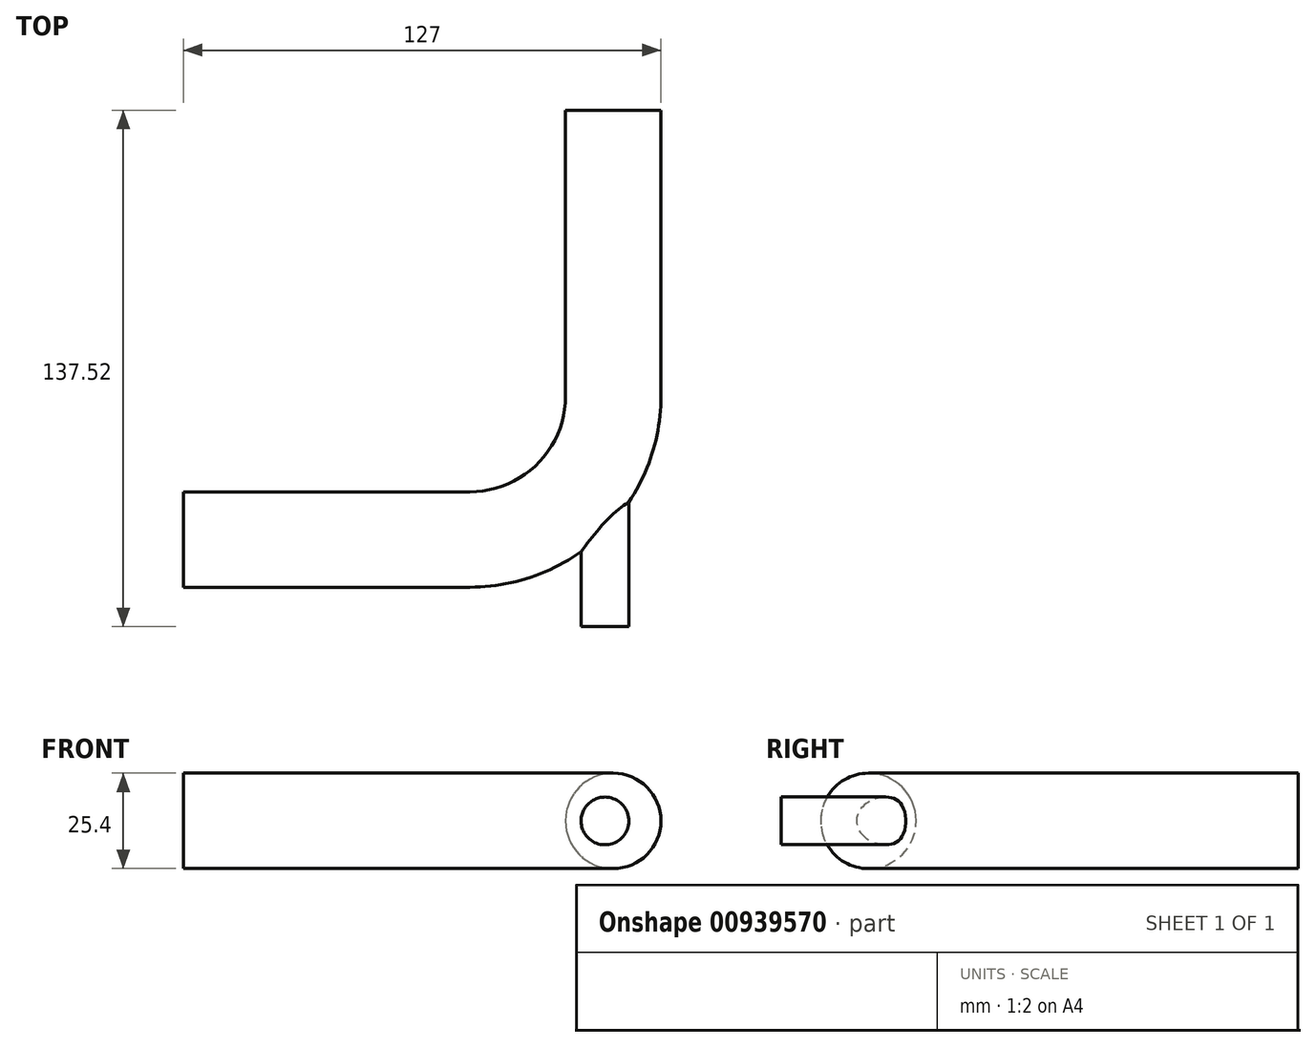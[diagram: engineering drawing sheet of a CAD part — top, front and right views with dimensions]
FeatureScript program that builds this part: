
annotation { "Feature Type Name" : "Feature", "Feature Type Description" : "" }
export const myFeature = defineFeature(function(context is Context, id is Id, definition is map)
    precondition{}
    {
        {
            var Q0;
            Q0=qCreatedBy(makeId("Top.planeOp"),FACE);
            var sketch = newSketch(context, id + "F0", { "sketchPlane" : qUnion([Q0])});
            skLineSegment(sketch, "E0", {"start": v(0, 0) * mm, "end": v(76.2, 0) * mm});
            skArc(sketch, "E1", {"start": v(76.2, 0) * mm, "mid": v(103.14, 11.16) * mm, "end": v(114.3, 38.1) * mm});
            skLineSegment(sketch, "E2", {"start": v(114.3, 38.1) * mm, "end": v(114.3, 114.3) * mm});
            skArc(sketch, "E3.0", {"start": v(76.2, -12.7) * mm, "mid": v(112.12, 2.18) * mm, "end": v(127, 38.1) * mm, "construction": true});
            skLineSegment(sketch, "E4", {"start": v(76.2, 38.1) * mm, "end": v(112.12, 2.18) * mm, "construction": true});
            skLineSegment(sketch, "E5", {"start": v(76.2, 38.1) * mm, "end": v(76.2, 0) * mm, "construction": true});
            skLineSegment(sketch, "E6", {"start": v(112.12, 2.18) * mm, "end": v(112.12, -23.22) * mm});
            skSolve(sketch);
        }
        {
            var Q0;
            Q0=qCreatedBy(makeId("Right.planeOp"),FACE);
            var sketch = newSketch(context, id + "F1", { "sketchPlane" : qUnion([Q0])});
            skCircle(sketch, "E7", {"center": v(0, 0) * mm, "radius": 12.7 * mm});
            skSolve(sketch);
        }
        {
            var Q0;
            Q0 = qSketchRegion(id + "F1", true);
            var Q1;
            Q1 = qConstructionFilter(qBodyType(qCreatedBy(id + "F1" ,EDGE), BodyType.WIRE), ConstructionObject.NO);
            var Q2;
            Q2=sQuery(id+"F0.wireOp",EDGE,"E0");
            var Q3;
            Q3=sQuery(id+"F0.wireOp",EDGE,"E1");
            var Q4;
            Q4=sQuery(id+"F0.wireOp",EDGE,"E2");
            sweep(context, id + "F2", {"profiles" : qUnion([Q0]), "surfaceProfiles" : qUnion([Q1]), "path" : qUnion([Q2, Q3, Q4])});
        }
        {
            var Q0;
            Q0=sQuery(id+"F0.wireOp",VERTEX,"E2.end");
            var Q1;
            Q1=sQuery(id+"F0.wireOp",EDGE,"E2");
            cPlane(context, id + "F3", {"entities" : qUnion([Q0, Q1]), "cplaneType" : CPlaneType.LINE_POINT, "offset" : 25.4 * mm, "width" : 152.4 * mm, "height" : 152.4 * mm});
        }
        {
            var Q0;
            Q0=sQuery(id+"F0.wireOp",VERTEX,"E6.end");
            var Q1;
            Q1=sQuery(id+"F0.wireOp",EDGE,"E2");
            cPlane(context, id + "F4", {"entities" : qUnion([Q0, Q1]), "cplaneType" : CPlaneType.LINE_POINT, "offset" : 25.4 * mm, "width" : 152.4 * mm, "height" : 152.4 * mm});
        }
        {
            var Q0;
            Q0=qCreatedBy(id+"F4.planeOp",FACE);
            var sketch = newSketch(context, id + "F5", { "sketchPlane" : qUnion([Q0])});
            skPoint(sketch, "E8.0", {"position": v(-112.12, 0) * mm});
            skCircle(sketch, "E9", {"center": v(-112.12, 0) * mm, "radius": 6.35 * mm});
            skSolve(sketch);
        }
        {
            var Q0;
            Q0=makeQuery(id+"F5.imprint","IMPRINT",FACE,{"disambiguationData":[TD([[makeQuery(id+"F5.imprint","IMPRINT",EDGE,{"derivedFrom":sQuery(id+"F5.wireOp",EDGE,"E9")}),1.0]])]});
            extrude(context, id + "F6", {"entities" : qUnion([Q0]), "operationType" : NewBodyOperationType.ADD, "endBound" : BoundingType.UP_TO_NEXT, "depth" : 25.4 * mm, "offsetDistance" : 25.4 * mm});
        }
    });
